# Revit family: Shower_Thermostatic_Trim-Grohe-Grandera-19940_Series
name_source: partatom
category: Plumbing Fixtures
revit_build: Autodesk Revit 2018 (Build: 20170223_1515(x64)
units: mm (PartAtom-declared; Revit-internal decimal feet)

## family parameters
Cut with Voids When Loaded = No
Host = Face
OmniClass Number = 23.45.05.14.17
OmniClass Title = Showers
Part Type = Normal
Room Calculation Point = No
Round Connector Dimension = Use Diameter
Shared = Yes

## types (2) — shared parameters
Assembly Code = D2010710
CW Connection = Yes
CWFU = 3
Default Elevation = 0"
Description = Grandera Custom Shower Thermostatic Valve Trim With Control Module, GROHE TurboStat, comes with multiple outlet custom shower applications and metal trim plate, also requires separate volume controls and GrohFlex 35026000 universal rough-In box.
Flow Rate = 14 gpm at 45 psi
HW Connection = Yes
HWFU = 3
Height = 6 11/16"
IAPMO Compliance = Energy Policy Act of 1992 and ASME A112.18.1/CSA B125.1
Installation Type = Wall Mounted
Manufacturer = Grohe
Min. Recommended Pressure = 15 psi (1.0 bar)
Price = Prices may vary. Please consult Manufacturer Representative for most up-to-date price list.
Product Documentation Link = https://americanstandard.box.com
Product Page URL = https://www.grohe.us
Revised Date = 07/17/2021
URL = https://www.grohe.us
Universal Rough-In Box = Sold Separately
Vent Connection = No
Volume Control = Sold Separately
WFU = 4
Waste Connection = No
Width = 6 11/16"

## per-type parameters (varying)
| type | Finish | Material |
| 19940000 | Metal-Grohe-000-StarLight Chrome | Metal-Grohe-000-StarLight Chrome |
| 19940EN0 | Metal-Grohe-EN0-Brushed Nickel Infinity Finish | Metal-Grohe-EN0-Brushed Nickel Infinity Finish |

note: column(s) folded — value = type name in every type: Model

## geometry (parser evidence)
native form markers: Sweep x2
no freeform markers — native parametric forms only
